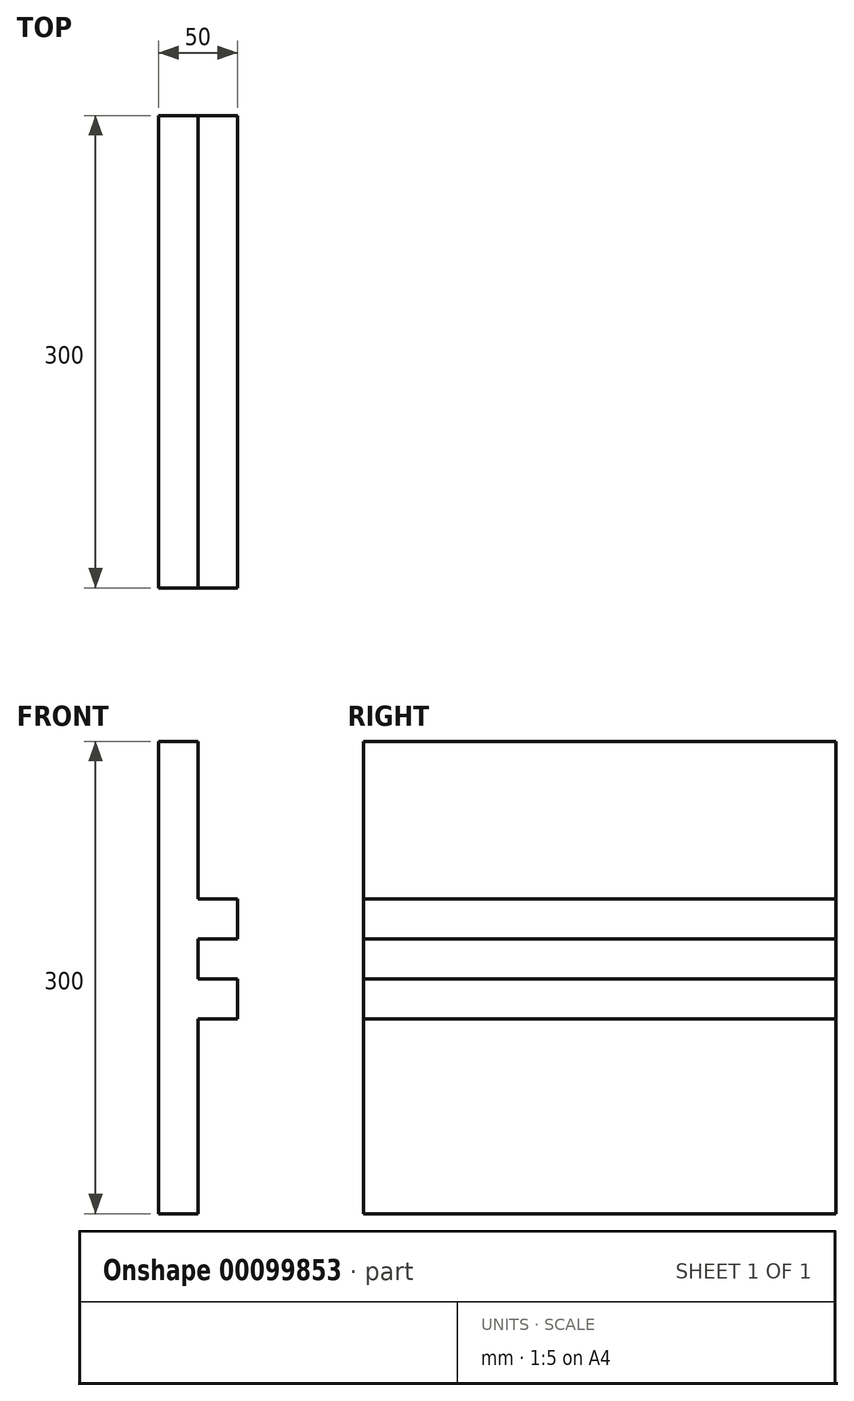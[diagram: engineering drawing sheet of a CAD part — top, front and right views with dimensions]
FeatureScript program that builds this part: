
annotation { "Feature Type Name" : "Feature", "Feature Type Description" : "" }
export const myFeature = defineFeature(function(context is Context, id is Id, definition is map)
    precondition{}
    {
        {
            var Q0;
            Q0=qCreatedBy(makeId("Right.planeOp"),FACE);
            var sketch = newSketch(context, id + "F0", { "sketchPlane" : qUnion([Q0])});
            skLineSegment(sketch, "E0.bottom", {"start": v(150, -150) * mm, "end": v(-150, -150) * mm});
            skLineSegment(sketch, "E0.top", {"start": v(150, 150) * mm, "end": v(-150, 150) * mm});
            skLineSegment(sketch, "E0.left", {"start": v(150, -150) * mm, "end": v(150, 150) * mm});
            skLineSegment(sketch, "E0.right", {"start": v(-150, -150) * mm, "end": v(-150, 150) * mm});
            skPoint(sketch, "E0.middle", {"position": v(0, 0) * mm});
            skSolve(sketch);
        }
        {
            var Q0;
            Q0=qSketchRegion(id+"F0",true);
            extrude(context, id + "F1", {"entities" : qUnion([Q0]), "depth" : 25 * mm});
        }
        {
            var Q0;
            Q0=makeQuery(id+"F1.opExtrude","CAP_FACE",FACE,{"disambiguationData":[OSD([sQuery(id+"F0.wireOp",EDGE,"E0.bottom"),sQuery(id+"F0.wireOp",EDGE,"E0.top"),sQuery(id+"F0.wireOp",EDGE,"E0.left"),sQuery(id+"F0.wireOp",EDGE,"E0.right")])],"isStart":false});
            var sketch = newSketch(context, id + "F2", { "sketchPlane" : qUnion([Q0])});
            skLineSegment(sketch, "E1.bottom", {"start": v(-150, 50) * mm, "end": v(150, 50) * mm});
            skLineSegment(sketch, "E1.top", {"start": v(-150, 24.6) * mm, "end": v(150, 24.6) * mm});
            skLineSegment(sketch, "E1.left", {"start": v(-150, 50) * mm, "end": v(-150, 24.6) * mm});
            skLineSegment(sketch, "E2", {"start": v(-150, 11.9) * mm, "end": v(150, 11.9) * mm, "construction": true});
            skLineSegment(sketch, "E3.MirrorCS", {"start": v(-150, -26.2) * mm, "end": v(-150, -0.8) * mm});
            skLineSegment(sketch, "E4.MirrorCS", {"start": v(-150, -0.8) * mm, "end": v(150, -0.8) * mm});
            skLineSegment(sketch, "E5.MirrorCS", {"start": v(-150, -26.2) * mm, "end": v(150, -26.2) * mm});
            skLineSegment(sketch, "E6", {"start": v(150, 50) * mm, "end": v(150, -26.2) * mm});
            skPoint(sketch, "E1.right.start.orphan", {"position": v(152.4, 50) * mm});
            skPoint(sketch, "E7.orphan", {"position": v(152.4, -26.2) * mm});
            skPoint(sketch, "E8.orphan", {"position": v(150, -0.8) * mm});
            skPoint(sketch, "E9.orphan", {"position": v(150, 24.6) * mm});
            skSolve(sketch);
        }
        {
            var Q0;
            Q0=qSketchRegion(id+"F2",true);
            extrude(context, id + "F3", {"entities" : qUnion([Q0]), "operationType" : NewBodyOperationType.ADD, "depth" : 25 * mm});
        }
    });
